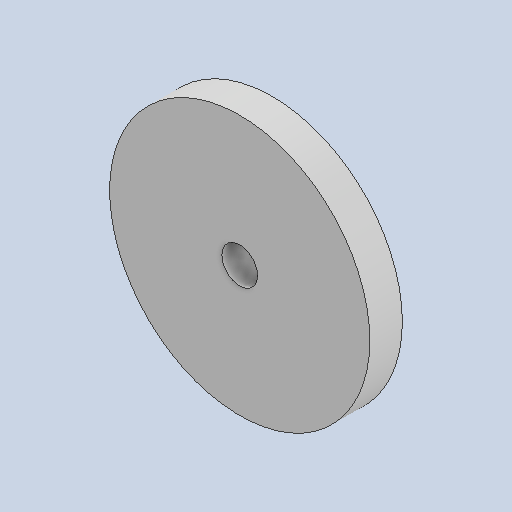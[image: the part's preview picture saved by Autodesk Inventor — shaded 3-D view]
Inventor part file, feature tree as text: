
AUTODESK INVENTOR PART (.ipt)
format: ipt  version: 2023 (Build 270158000, 158)  size: 143,872 bytes
history: native  units: mm
features: other x3, extrude x1, sketch x1, reference x1
ambient origin geometry x8: Origin, YZ Plane, XZ Plane, XY Plane, X Axis, Y Axis, Z Axis, Center Point
bodies: Solid1 (feature_tree)
feature tree (6):
  extrude  "Extrusion1"  Depth=5.0mm
  sketch  "Sketch1"  dims[d0=5.5mm d1=40.0mm d2=5.0mm d3=0.0mm]
  reference  "Reference1"
  other  "<userpath>\OneDrive\Namizje\school\4. letnik\Matura\Izdelovanje\3D model\3D_skenner.iam"
  other  "3D_skenner.iam"
  other  "motor_sample:1"
